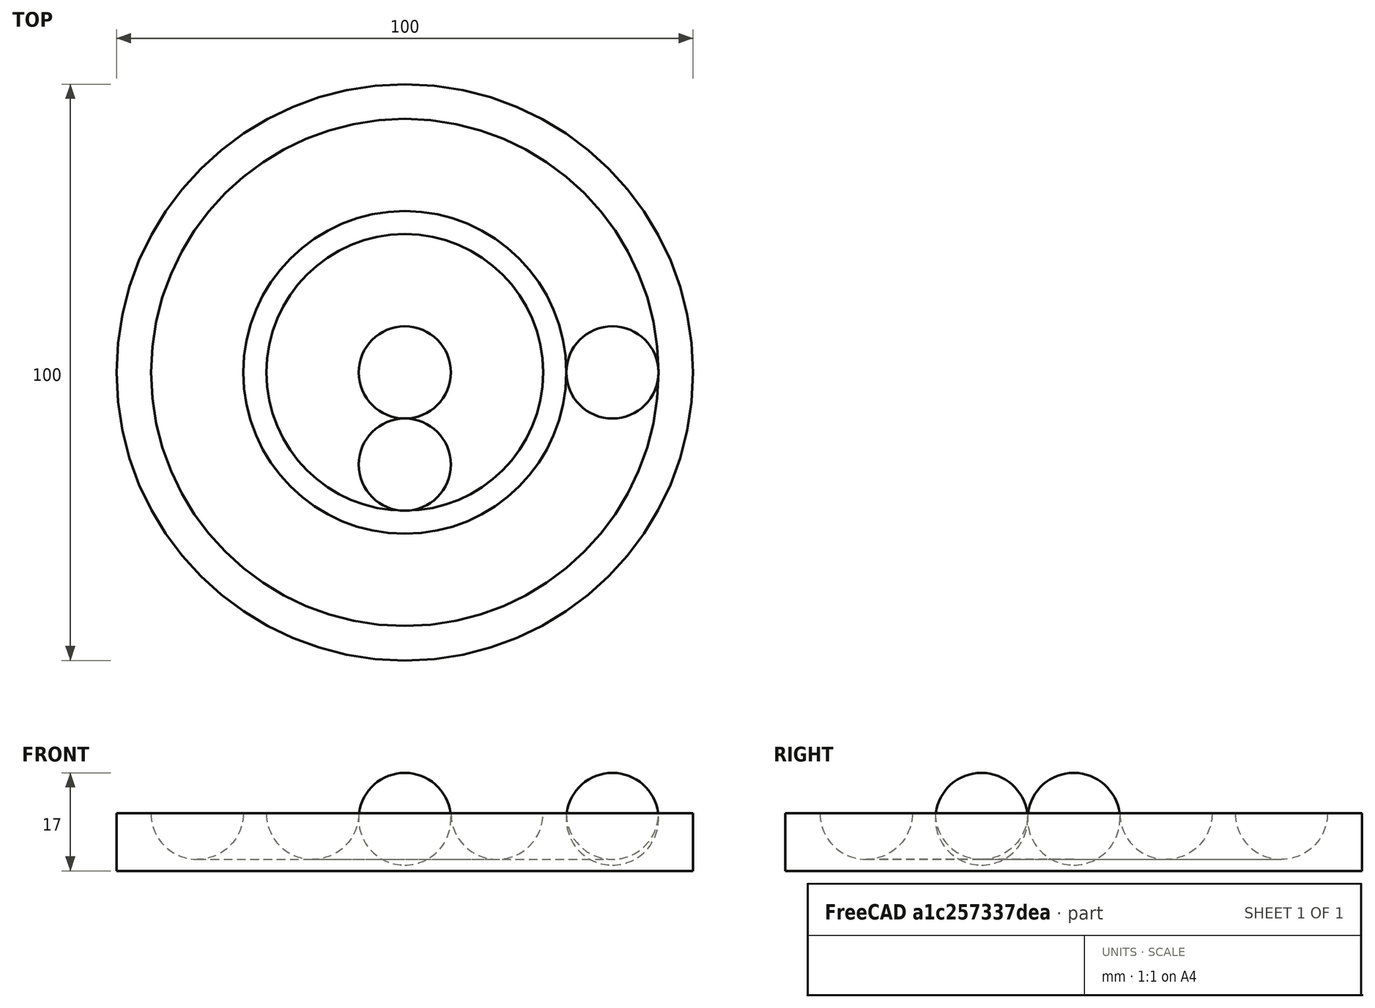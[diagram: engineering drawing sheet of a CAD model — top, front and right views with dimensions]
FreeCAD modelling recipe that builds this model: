
FCSTD DOCUMENT  (FreeCAD 0.21R33694 (Git))
Label: OJT1_T15R02.portacaniques
License: All rights reserved
LicenseURL: http://en.wikipedia.org/wiki/All_rights_reserved
objects: Part::Torus×2, Part::Sphere×2, Part::Cylinder×1, Part::Fuse×1, Part::Cut×1
note: 7 computed .brp shape members not serialized (recipe doc carries the construction recipe); baked Part::Feature solids carry a one-line shape summary decoded from their .brp

FEATURE [Part::Cylinder] Cylinder  label="Cilindre"
  Angle = 360
  AttacherType = Attacher::AttachEngine3D
  FirstAngle = 0
  Height = 10
  Radius = 50
  SecondAngle = 0
FEATURE [Part::Torus] Torus
  Angle1 = -180
  Angle2 = 180
  Angle3 = 360
  AttacherType = Attacher::AttachEngine3D
  Placement = pos=(0,0,10) rot=(0,0,1;0rad)
  Radius1 = 16
  Radius2 = 8
FEATURE [Part::Torus] Torus001
  Angle1 = -180
  Angle2 = 180
  Angle3 = 360
  AttacherType = Attacher::AttachEngine3D
  Placement = pos=(0,0,10) rot=(0,0,1;0rad)
  Radius1 = 36
  Radius2 = 8
FEATURE [Part::Fuse] Fusion
  Base = -> Torus
  Refine = true
  Tool = -> Torus001
FEATURE [Part::Cut] Cut
  Base = -> Cylinder
  Refine = true
  Tool = -> Fusion
FEATURE [Part::Sphere] Sphere  label="Esfera"
  Angle1 = -90
  Angle2 = 90
  Angle3 = 360
  AttacherType = Attacher::AttachEngine3D
  Placement = pos=(36,0,9) rot=(0,0,1;0rad)
  Radius = 8
FEATURE [Part::Sphere] Sphere001  label="Esfera001"
  Angle1 = -90
  Angle2 = 90
  Angle3 = 360
  AttacherType = Attacher::AttachEngine3D
  Placement = pos=(0,-16,9) rot=(0,0,1;0rad)
  Radius = 8
